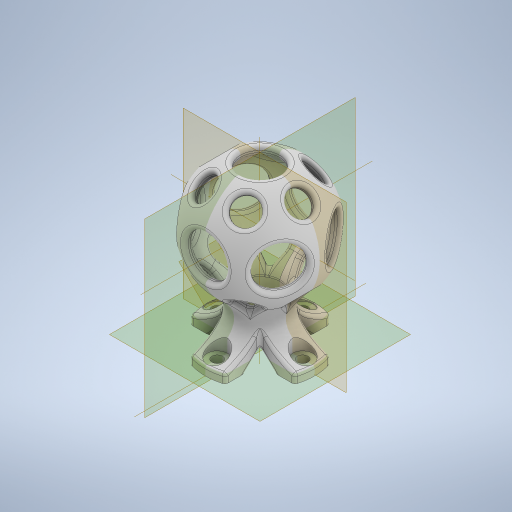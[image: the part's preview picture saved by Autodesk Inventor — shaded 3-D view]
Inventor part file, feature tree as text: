
AUTODESK INVENTOR PART (.ipt)
format: ipt  version: 2023 (Build 270158000, 158)  size: 2,082,304 bytes
history: native  units: in
note: dims shown in document units (in); Inventor stores cm internally (conversion verified against a paired STEP export)
features: other x9, sketch x8, pattern_circular x7, extrude x5, fillet x5, plane x4, revolve x3
ambient origin geometry x8: Origin, YZ Plane, XZ Plane, XY Plane, X Axis, Y Axis, Z Axis, Center Point
bodies: Solid1 (feature_tree)
feature tree (41):
  other  "Blocks"
  revolve  "Revolution1"  Angle=90.0deg
  extrude  "Extrusion1"  TaperAngle=360.0deg  [1 undecoded]
  sketch  "Sketch4"  dims[d6=0.9843in d7=1.5748in d9=360.0deg]
  plane  "Work Plane1"
  extrude  "Extrusion2"  Depth=1.5748in TaperAngle=360.0deg
  plane  "Work Plane2"
  sketch  "Sketch5"  dims[d11=0.2441in d12=0.4724in d13=0.0in]
  other  "Work Point1"
  other  "Work Point2"
  plane  "Work Plane3"
  other  "Work Axis2"
  other  "Work Axis3"
  revolve  "Revolution3"  [1 undecoded]
  other  "Work Axis4"
  pattern_circular  "Circular Pattern1"  Count=4 Angle=360.0deg
  revolve  "Revolution5"  [1 undecoded]
  pattern_circular  "Circular Pattern3"  Count=6  [1 undecoded]
  extrude  "Extrusion3"  Depth=0.9449in
  extrude  "Extrusion4"  Depth=0.0787in TaperAngle=360.0deg
  pattern_circular  "Circular Pattern4"  Count=6  [1 undecoded]
  plane  "Work Plane5"
  extrude  "Extrusion6"  Depth=0.0787in
  pattern_circular  "Circular Pattern6"  [2 undecoded]
  fillet  "Fillet1"  [1 undecoded]
  pattern_circular  "Circular Pattern7"  Angle=360.0deg  [1 undecoded]
  fillet  "Fillet2"  Radius=2.3622in
  fillet  "Fillet3"  [1 undecoded]
  pattern_circular  "Circular Pattern8"  Count=2  [1 undecoded]
  fillet  "Fillet4"  Radius=0.3937in
  pattern_circular  "Circular Pattern9"  Angle=45.0deg  [1 undecoded]
  fillet  "Fillet8"  Radius=0.7874in
  sketch  "Sketch2"  dims[d2=1.2598in d3=90.0deg]
  other  "construction"
  sketch  "Sketch3"  dims[d4=0.1969in d5=360.0deg]
  other  "Work Axis1"
  sketch  "Sketch8"  dims[d14=0.4724in d15=1.5748in d17=360.0deg]
  sketch  "Sketch9"  dims[d19=-0.1969in d20=0.4724in d21=0.0in d22=2.3622in]
  sketch  "Sketch11"  dims[d23=0.1969in d27=0.9449in]
  sketch  "Sketch13"  dims[d28=360.0deg d29=2.3622in d30=360.0deg d39=2.3622in d40=2.3622in d41=0.3937in d42=45.0deg d43=360.0deg d44=2.3622in d45=360.0deg d47=0.0in d48=0.0in d49=0.7874in d50=0.3937in d51=45.0deg d52=0.7874in d53=0.0in d54=1.5748in d55=360.0deg d66=1.1811in d67=0.0in d68=2.3622in d69=360.0deg d73=0.0787in d74=1.1417in d75=0.0787in d76=2.3622in d77=360.0deg d79=0.0787in d80=0.0787in d81=2.3622in d82=360.0deg d84=0.0787in d86=1.5748in d87=360.0deg d91=0.0787in d92=0.1575in d24=0.0344in d25=0.0344in d57=0.0in d58=0.0in d59=0.0in d60=0.0in d85=0.0in]
  other  "construction:1"
note: 12 required parameter values undecoded (feature->parameter linkage not recoverable at this tier; creation-order binding heuristic only, values carry confidence <= 0.55)